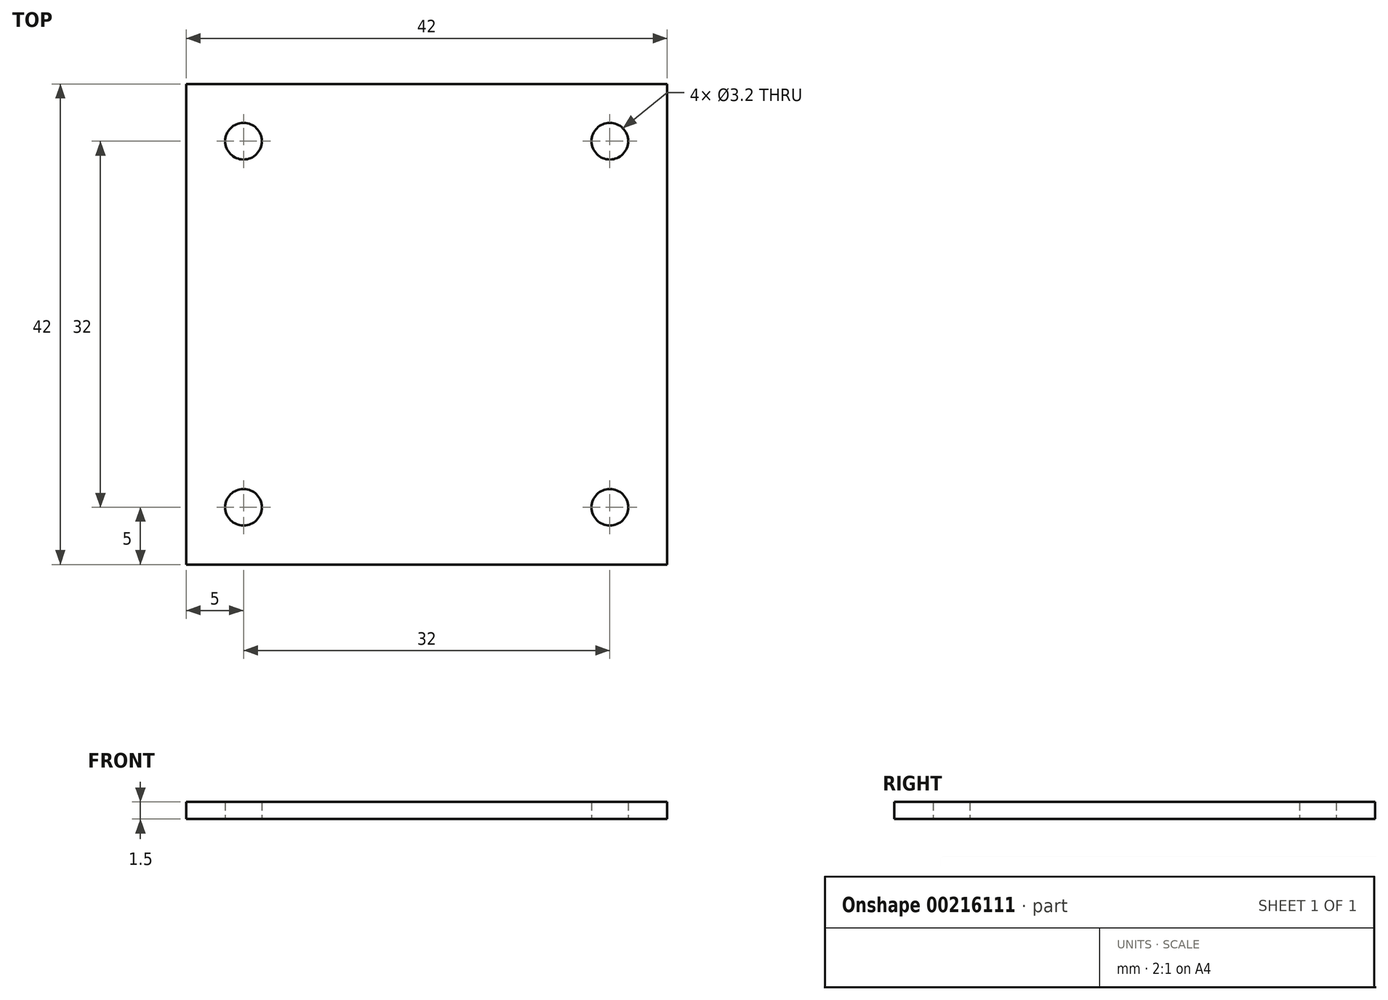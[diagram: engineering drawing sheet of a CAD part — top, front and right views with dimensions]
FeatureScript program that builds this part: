
annotation { "Feature Type Name" : "Feature", "Feature Type Description" : "" }
export const myFeature = defineFeature(function(context is Context, id is Id, definition is map)
    precondition{}
    {
        {
            var Q0;
            Q0=qCreatedBy(makeId("Top.planeOp"),FACE);
            var sketch = newSketch(context, id + "F0", { "sketchPlane" : qUnion([Q0])});
            skLineSegment(sketch, "E0.bottom", {"start": v(-21, 21) * mm, "end": v(21, 21) * mm});
            skLineSegment(sketch, "E0.top", {"start": v(-21, -21) * mm, "end": v(21, -21) * mm});
            skLineSegment(sketch, "E0.left", {"start": v(-21, 21) * mm, "end": v(-21, -21) * mm});
            skLineSegment(sketch, "E0.right", {"start": v(21, 21) * mm, "end": v(21, -21) * mm});
            skLineSegment(sketch, "E1", {"start": v(0, 0) * mm, "end": v(0, 5.67) * mm, "construction": true});
            skLineSegment(sketch, "E2", {"start": v(0, 0) * mm, "end": v(-6.97, 0) * mm, "construction": true});
            skLineSegment(sketch, "E3.bottom", {"start": v(-16, 16) * mm, "end": v(16, 16) * mm, "construction": true});
            skLineSegment(sketch, "E3.top", {"start": v(-16, -16) * mm, "end": v(16, -16) * mm, "construction": true});
            skLineSegment(sketch, "E3.left", {"start": v(-16, 16) * mm, "end": v(-16, -16) * mm, "construction": true});
            skLineSegment(sketch, "E3.right", {"start": v(16, 16) * mm, "end": v(16, -16) * mm, "construction": true});
            skCircle(sketch, "E4", {"center": v(-16, 16) * mm, "radius": 1.6 * mm});
            skCircle(sketch, "E5", {"center": v(16, 16) * mm, "radius": 1.6 * mm});
            skCircle(sketch, "E6", {"center": v(16, -16) * mm, "radius": 1.6 * mm});
            skCircle(sketch, "E7", {"center": v(-16, -16) * mm, "radius": 1.6 * mm});
            skSolve(sketch);
        }
        {
            var Q0;
            Q0=makeQuery(id+"F0.imprint","IMPRINT",FACE,{"disambiguationData":[TD([[makeQuery(id+"F0.imprint","IMPRINT",EDGE,{"derivedFrom":sQuery(id+"F0.wireOp",EDGE,"E0.bottom")}),-1.0]])]});
            extrude(context, id + "F1", {"entities" : qUnion([Q0]), "depth" : 1.5 * mm});
        }
    });
